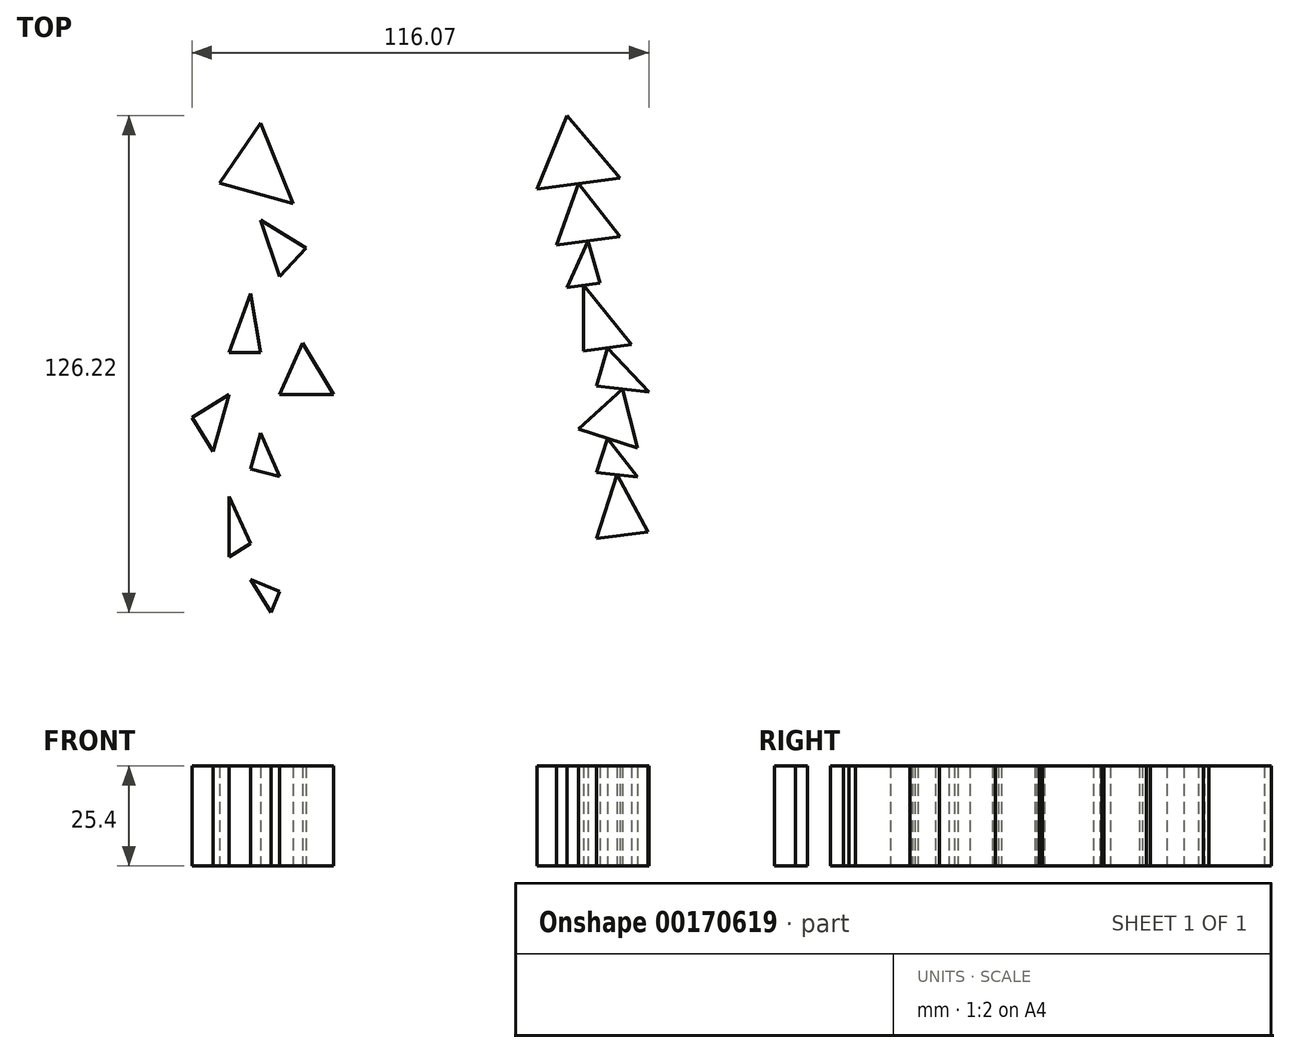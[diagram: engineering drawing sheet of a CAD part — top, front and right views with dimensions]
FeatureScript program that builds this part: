
annotation { "Feature Type Name" : "Feature", "Feature Type Description" : "" }
export const myFeature = defineFeature(function(context is Context, id is Id, definition is map)
    precondition{}
    {
        {
            var Q0;
            Q0=qCreatedBy(makeId("Top.planeOp"),FACE);
            var sketch = newSketch(context, id + "F0", { "sketchPlane" : qUnion([Q0])});
            skLineSegment(sketch, "E0", {"start": v(-50.39, 47.94) * mm, "end": v(-60.77, 32.68) * mm});
            skLineSegment(sketch, "E1", {"start": v(-60.77, 32.68) * mm, "end": v(-42.14, 27.48) * mm});
            skLineSegment(sketch, "E2", {"start": v(-42.14, 27.48) * mm, "end": v(-50.39, 47.94) * mm});
            skLineSegment(sketch, "E3", {"start": v(-50.39, 23.2) * mm, "end": v(-45.5, 8.86) * mm});
            skLineSegment(sketch, "E4", {"start": v(-45.5, 8.86) * mm, "end": v(-38.78, 16.19) * mm});
            skLineSegment(sketch, "E5", {"start": v(-38.78, 16.19) * mm, "end": v(-50.39, 23.2) * mm});
            skLineSegment(sketch, "E6", {"start": v(-52.83, 4.58) * mm, "end": v(-58.33, -10.38) * mm});
            skLineSegment(sketch, "E7", {"start": v(-58.33, -10.38) * mm, "end": v(-50.39, -10.38) * mm});
            skLineSegment(sketch, "E8", {"start": v(-50.39, -10.38) * mm, "end": v(-52.83, 4.58) * mm});
            skLineSegment(sketch, "E9", {"start": v(-39.7, -7.94) * mm, "end": v(-45.5, -21.07) * mm});
            skLineSegment(sketch, "E10", {"start": v(-45.5, -21.07) * mm, "end": v(-31.76, -21.07) * mm});
            skLineSegment(sketch, "E11", {"start": v(-31.76, -21.07) * mm, "end": v(-39.7, -7.94) * mm});
            skLineSegment(sketch, "E12", {"start": v(-50.39, -30.84) * mm, "end": v(-52.83, -40) * mm});
            skLineSegment(sketch, "E13", {"start": v(-52.83, -40) * mm, "end": v(-45.5, -41.96) * mm});
            skLineSegment(sketch, "E14", {"start": v(-45.5, -41.96) * mm, "end": v(-50.39, -30.84) * mm});
            skLineSegment(sketch, "E15", {"start": v(-58.33, -21.07) * mm, "end": v(-67.8, -26.87) * mm});
            skLineSegment(sketch, "E16", {"start": v(-67.8, -26.87) * mm, "end": v(-62.45, -35.59) * mm});
            skLineSegment(sketch, "E17", {"start": v(-62.45, -35.59) * mm, "end": v(-58.33, -21.07) * mm});
            skLineSegment(sketch, "E18", {"start": v(-58.33, -47.03) * mm, "end": v(-58.33, -62.3) * mm});
            skLineSegment(sketch, "E19", {"start": v(-58.33, -62.3) * mm, "end": v(-52.83, -58.93) * mm});
            skLineSegment(sketch, "E20", {"start": v(-52.83, -58.93) * mm, "end": v(-58.33, -47.03) * mm});
            skLineSegment(sketch, "E21", {"start": v(-52.83, -68.1) * mm, "end": v(-47.72, -76.44) * mm});
            skLineSegment(sketch, "E22", {"start": v(-47.72, -76.44) * mm, "end": v(-45.5, -71.15) * mm});
            skLineSegment(sketch, "E23", {"start": v(-45.5, -71.15) * mm, "end": v(-52.83, -68.1) * mm});
            skSolve(sketch);
        }
        {
            var Q0;
            Q0 = qSketchRegion(id + "F0", true);
            extrude(context, id + "F1", {"entities" : qUnion([Q0]), "depth" : 25.4 * mm});
        }
        {
            var Q0;
            Q0=qCreatedBy(makeId("Top.planeOp"),FACE);
            var sketch = newSketch(context, id + "F2", { "sketchPlane" : qUnion([Q0])});
            skLineSegment(sketch, "E24", {"start": v(27.48, 49.78) * mm, "end": v(19.85, 31.15) * mm});
            skLineSegment(sketch, "E25", {"start": v(19.85, 31.15) * mm, "end": v(40.92, 33.9) * mm});
            skLineSegment(sketch, "E26", {"start": v(40.92, 33.9) * mm, "end": v(27.48, 49.78) * mm});
            skLineSegment(sketch, "E27", {"start": v(30.39, 32.52) * mm, "end": v(24.81, 16.91) * mm});
            skLineSegment(sketch, "E28", {"start": v(24.81, 16.91) * mm, "end": v(40.92, 19.01) * mm});
            skLineSegment(sketch, "E29", {"start": v(40.92, 19.01) * mm, "end": v(30.39, 32.52) * mm});
            skLineSegment(sketch, "E30", {"start": v(32.87, 17.96) * mm, "end": v(27.48, 6.14) * mm});
            skLineSegment(sketch, "E31", {"start": v(27.48, 6.14) * mm, "end": v(35.85, 7.23) * mm});
            skLineSegment(sketch, "E32", {"start": v(35.85, 7.23) * mm, "end": v(32.87, 17.96) * mm});
            skLineSegment(sketch, "E33", {"start": v(31.67, 6.69) * mm, "end": v(31.67, -10.02) * mm});
            skLineSegment(sketch, "E34", {"start": v(31.67, -10.02) * mm, "end": v(43.88, -8.43) * mm});
            skLineSegment(sketch, "E35", {"start": v(43.88, -8.43) * mm, "end": v(31.67, 6.69) * mm});
            skLineSegment(sketch, "E36", {"start": v(37.77, -9.22) * mm, "end": v(35, -18.87) * mm});
            skLineSegment(sketch, "E37", {"start": v(35, -18.87) * mm, "end": v(48.28, -20.4) * mm});
            skLineSegment(sketch, "E38", {"start": v(48.28, -20.4) * mm, "end": v(37.77, -9.22) * mm});
            skLineSegment(sketch, "E39", {"start": v(41.65, -19.64) * mm, "end": v(30.39, -29.84) * mm});
            skLineSegment(sketch, "E40", {"start": v(30.39, -29.84) * mm, "end": v(45.4, -34.64) * mm});
            skLineSegment(sketch, "E41", {"start": v(45.4, -34.64) * mm, "end": v(41.65, -19.64) * mm});
            skLineSegment(sketch, "E42", {"start": v(37.77, -32.2) * mm, "end": v(35, -40.83) * mm});
            skLineSegment(sketch, "E43", {"start": v(35, -40.83) * mm, "end": v(45.4, -42.03) * mm});
            skLineSegment(sketch, "E44", {"start": v(45.4, -42.03) * mm, "end": v(37.77, -32.2) * mm});
            skLineSegment(sketch, "E45", {"start": v(40.2, -41.43) * mm, "end": v(35, -57.64) * mm});
            skLineSegment(sketch, "E46", {"start": v(35, -57.64) * mm, "end": v(48.04, -55.94) * mm});
            skLineSegment(sketch, "E47", {"start": v(48.04, -55.94) * mm, "end": v(40.2, -41.43) * mm});
            skSolve(sketch);
        }
        {
            var Q0;
            Q0 = qSketchRegion(id + "F2", true);
            extrude(context, id + "F3", {"entities" : qUnion([Q0]), "depth" : 25.4 * mm});
        }
    });
